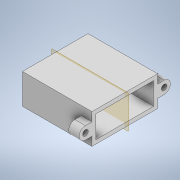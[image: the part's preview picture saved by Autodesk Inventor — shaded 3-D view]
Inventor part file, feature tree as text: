
AUTODESK INVENTOR PART (.ipt)
format: ipt  version: 2021 (Build 250183000, 183)  size: 163,328 bytes
history: native  units: mm
features: extrude x4, sketch x3, projected_geometry x2, mirror x1
ambient origin geometry x8: Origin, YZ Plane, XZ Plane, XY Plane, X Axis, Y Axis, Z Axis, Center Point
bodies: Body1 (feature_tree)
feature tree (10):
  sketch  "Sketch2"  dims[d8=50.0mm d9=23.0mm]
  extrude  "Extrusion3"  Depth=23.0mm
  extrude  "Extrusion4"  Depth=3.0mm
  extrude  "Extrusion7"  Depth=17.0mm
  extrude  "Extrusion8"  Depth=3.0mm TaperAngle=0.0deg
  mirror  "Mirror1"
  sketch  "Sketch5"  dims[d10=3.0mm d11=3.0mm]
  projected_geometry  "Projected Loop3"
  sketch  "Sketch6"  dims[d12=3.0mm d13=17.0mm d14=3.0mm d15=0.0mm d16=53.0mm d17=0.0mm d32=9.5mm d33=5.0mm d34=8.0mm d35=0.0mm d36=7.2mm d37=4.0mm d38=0.0mm d39=4.2mm]
  projected_geometry  "Projected Loop4"
